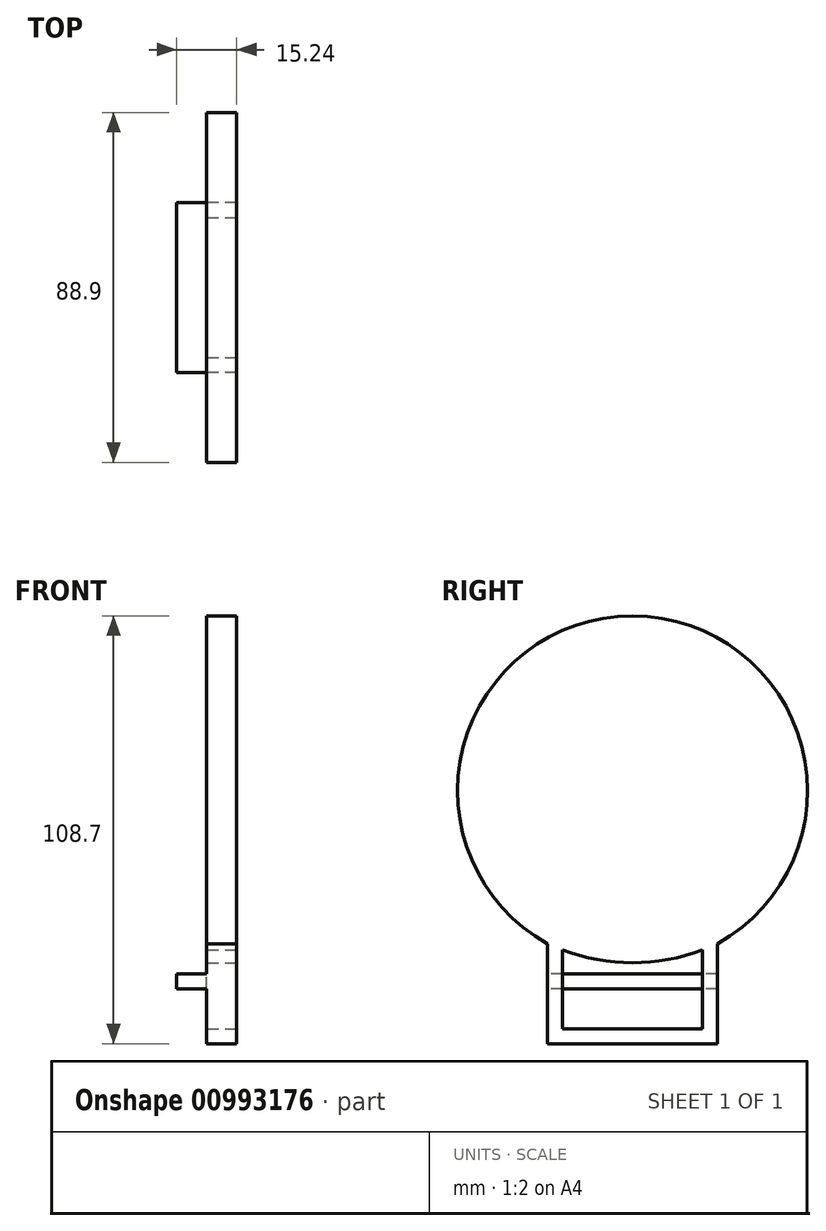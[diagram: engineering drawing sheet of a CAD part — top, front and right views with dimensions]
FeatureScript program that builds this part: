
annotation { "Feature Type Name" : "Feature", "Feature Type Description" : "" }
export const myFeature = defineFeature(function(context is Context, id is Id, definition is map)
    precondition{}
    {
        {
            var Q0;
            Q0=qCreatedBy(makeId("Right.planeOp"),FACE);
            var sketch = newSketch(context, id + "F0", { "sketchPlane" : qUnion([Q0])});
            skCircle(sketch, "E0", {"center": v(-42.83, -236.19) * mm, "radius": 44.45 * mm});
            skCircle(sketch, "E1", {"center": v(-42.83, -236.19) * mm, "radius": 31.75 * mm});
            skLineSegment(sketch, "E2.bottom", {"start": v(-21.24, -275.04) * mm, "end": v(-64.42, -275.04) * mm});
            skLineSegment(sketch, "E2.top", {"start": v(-21.24, -300.44) * mm, "end": v(-64.42, -300.44) * mm});
            skLineSegment(sketch, "E2.left", {"start": v(-21.24, -275.04) * mm, "end": v(-21.24, -300.44) * mm});
            skLineSegment(sketch, "E2.right", {"start": v(-64.42, -275.04) * mm, "end": v(-64.42, -300.44) * mm});
            skPoint(sketch, "E2.middle", {"position": v(-42.83, -287.74) * mm});
            skLineSegment(sketch, "E3.bottom", {"start": v(-21.24, -286.47) * mm, "end": v(-64.42, -286.47) * mm});
            skLineSegment(sketch, "E3.top", {"start": v(-21.24, -282.66) * mm, "end": v(-64.42, -282.66) * mm});
            skLineSegment(sketch, "E3.left", {"start": v(-21.24, -286.47) * mm, "end": v(-21.24, -282.66) * mm});
            skLineSegment(sketch, "E3.right", {"start": v(-64.42, -286.47) * mm, "end": v(-64.42, -282.66) * mm});
            skSolve(sketch);
        }
        {
            var Q0;
            {var subQ0=sQuery(id+"F0.wireOp",EDGE,"E2.bottom");Q0=makeQuery(id+"F0.imprint","IMPRINT",FACE,{"disambiguationData":[TD([[makeQuery(id+"F0.imprint","IMPRINT",EDGE,{"derivedFrom":subQ0}),1.0]])]});}
            var Q1;
            Q1=makeQuery(id+"F0.imprint","IMPRINT",FACE,{"disambiguationData":[TD([[makeQuery(id+"F0.imprint","IMPRINT",EDGE,{"derivedFrom":sQuery(id+"F0.wireOp",EDGE,"E2.top")}),-1.0]])]});
            var Q2;
            {var subQ6=sQuery(id+"F0.wireOp",EDGE,"E3.top");Q2=makeQuery(id+"F0.imprint","IMPRINT",FACE,{"disambiguationData":[TD([[makeQuery(id+"F0.imprint","IMPRINT",EDGE,{"derivedFrom":subQ6}),-1.0]])]});}
            var Q3;
            Q3=makeQuery(id+"F0.imprint","IMPRINT",FACE,{"disambiguationData":[TD([[makeQuery(id+"F0.imprint","IMPRINT",EDGE,{"derivedFrom":sQuery(id+"F0.wireOp",EDGE,"E3.bottom")}),-1.0]])]});
            var Q4;
            Q4=makeQuery(id+"F0.imprint","IMPRINT",FACE,{"disambiguationData":[TD([[makeQuery(id+"F0.imprint","IMPRINT",EDGE,{"derivedFrom":sQuery(id+"F0.wireOp",EDGE,"E1")}),1.0]])]});
            var Q5;
            Q5=makeQuery(id+"F0.imprint","IMPRINT",FACE,{"disambiguationData":[TD([[makeQuery(id+"F0.imprint","IMPRINT",EDGE,{"derivedFrom":sQuery(id+"F0.wireOp",EDGE,"E1")}),-1.0]])]});
            extrude(context, id + "F1", {"entities" : qUnion([Q0, Q1, Q2, Q3, Q4, Q5]), "depth" : 7.62 * mm, "offsetDistance" : 25.4 * mm});
        }
        {
            var Q0;
            Q0=makeQuery(id+"F1.opExtrude","CAP_FACE",FACE,{"disambiguationData":[OSD([sQuery(id+"F0.wireOp",EDGE,"E0"),sQuery(id+"F0.wireOp",EDGE,"E1"),sQuery(id+"F0.wireOp",EDGE,"E2.top"),sQuery(id+"F0.wireOp",EDGE,"E2.left"),sQuery(id+"F0.wireOp",EDGE,"E2.right")])],"isStart":false});
            var sketch = newSketch(context, id + "F2", { "sketchPlane" : qUnion([Q0])});
            skLineSegment(sketch, "E4.bottom", {"start": v(-60.6, -296.63) * mm, "end": v(-25.05, -296.63) * mm});
            skLineSegment(sketch, "E4.top", {"start": v(-60.6, -275.04) * mm, "end": v(-25.05, -275.04) * mm});
            skLineSegment(sketch, "E4.left", {"start": v(-60.6, -296.63) * mm, "end": v(-60.6, -275.04) * mm});
            skLineSegment(sketch, "E4.right", {"start": v(-25.05, -296.63) * mm, "end": v(-25.05, -275.04) * mm});
            skArc(sketch, "E5", {"start": v(-64.42, -275.04) * mm, "mid": v(-42.83, -279.86) * mm, "end": v(-21.24, -275.04) * mm});
            skSolve(sketch);
        }
        {
            var Q0;
            Q0=makeQuery(id+"F0.imprint","IMPRINT",FACE,{"disambiguationData":[TD([[makeQuery(id+"F0.imprint","IMPRINT",EDGE,{"derivedFrom":sQuery(id+"F0.wireOp",EDGE,"E1")}),-1.0]])]});
            extrude(context, id + "F3", {"entities" : qUnion([Q0]), "operationType" : NewBodyOperationType.ADD, "depth" : 7.62 * mm, "offsetDistance" : 25.4 * mm});
        }
        {
            var Q0;
            {var subQ0=sQuery(id+"F2.wireOp",EDGE,"E4.bottom");Q0=makeQuery(id+"F2.imprint","IMPRINT",FACE,{"disambiguationData":[TD([[makeQuery(id+"F2.imprint","IMPRINT",EDGE,{"derivedFrom":subQ0}),1.0]])]});}
            extrude(context, id + "F4", {"entities" : qUnion([Q0]), "operationType" : NewBodyOperationType.REMOVE, "oppositeDirection" : true, "depth" : 76.2 * mm, "offsetDistance" : 25.4 * mm});
        }
        {
            var Q0;
            Q0=makeQuery(id+"F0.imprint","IMPRINT",FACE,{"disambiguationData":[TD([[makeQuery(id+"F0.imprint","IMPRINT",EDGE,{"derivedFrom":sQuery(id+"F0.wireOp",EDGE,"E3.bottom")}),-1.0]])]});
            extrude(context, id + "F5", {"entities" : qUnion([Q0]), "operationType" : NewBodyOperationType.ADD, "oppositeDirection" : true, "depth" : 7.62 * mm, "offsetDistance" : 25.4 * mm});
        }
    });
